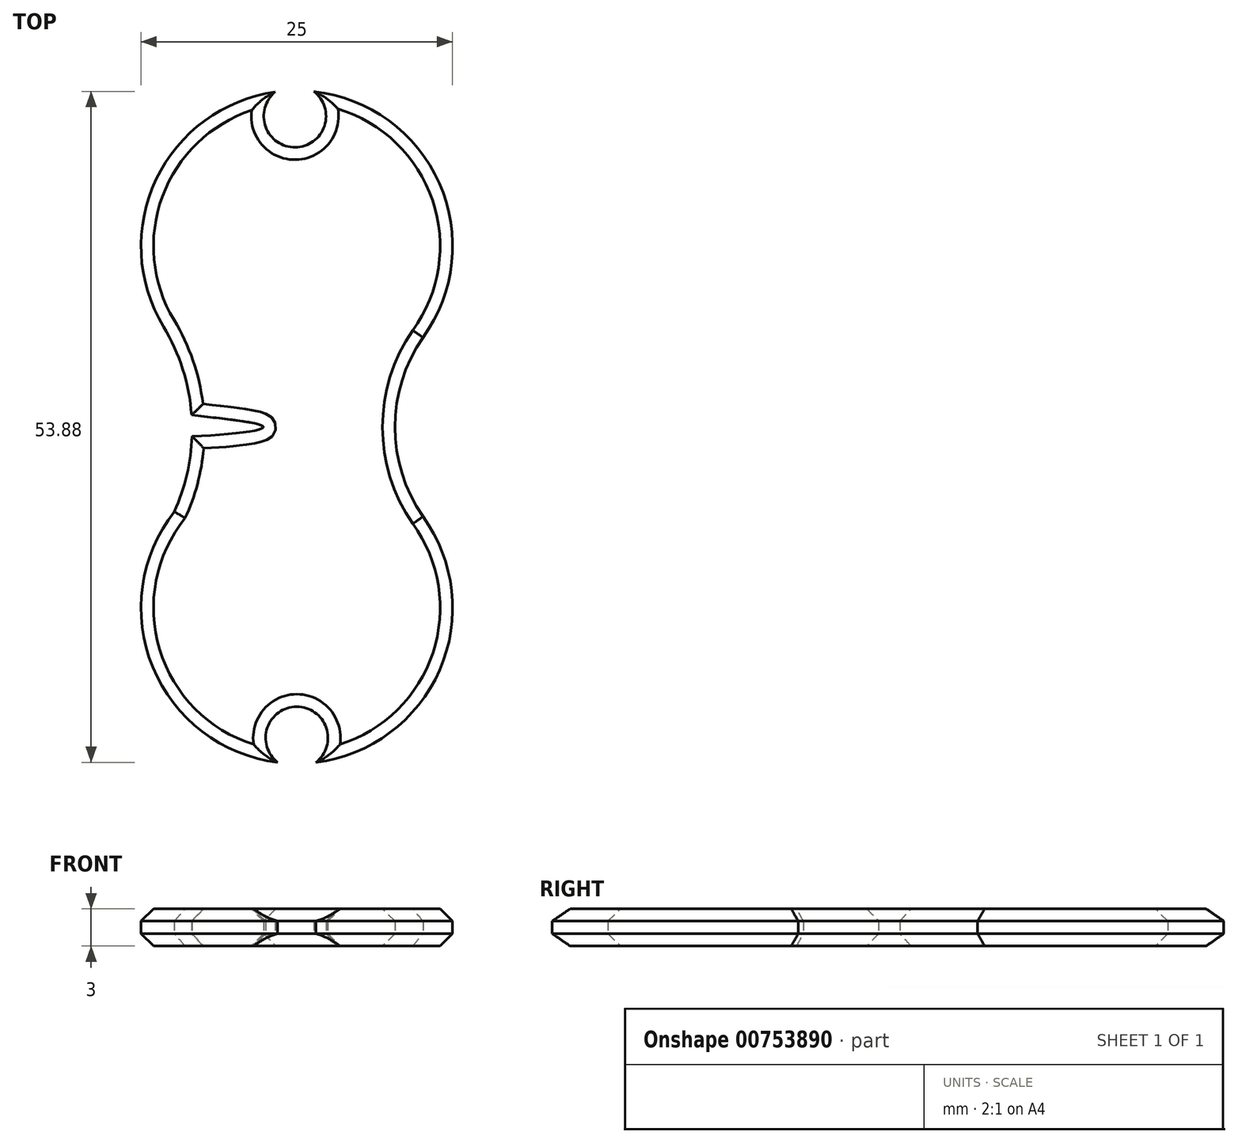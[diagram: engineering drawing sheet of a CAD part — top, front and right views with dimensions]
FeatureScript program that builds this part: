
annotation { "Feature Type Name" : "Feature", "Feature Type Description" : "" }
export const myFeature = defineFeature(function(context is Context, id is Id, definition is map)
    precondition{}
    {
        {
            var Q0;
            Q0=qCreatedBy(makeId("Top.planeOp"),FACE);
            var sketch = newSketch(context, id + "F0", { "sketchPlane" : qUnion([Q0])});
            skArc(sketch, "E0", {"start": v(10.12, 7.19) * mm, "mid": v(11.43, 19.59) * mm, "end": v(1.37, 26.95) * mm});
            skArc(sketch, "E1.MirrorC", {"start": v(10.12, -7.19) * mm, "mid": v(11.46, -19.51) * mm, "end": v(1.53, -26.93) * mm});
            skArc(sketch, "E2", {"start": v(-9.82, -6.8) * mm, "mid": v(-8.82, -3.83) * mm, "end": v(-8.41, -0.74) * mm});
            skArc(sketch, "E3.MirrorC", {"start": v(10.12, -7.19) * mm, "mid": v(8.45, -3.77) * mm, "end": v(7.88, 0) * mm});
            skPoint(sketch, "E4.start.orphan", {"position": v(0, 2.02) * mm});
            skPoint(sketch, "E5.start.orphan", {"position": v(-26.08, 0) * mm});
            skArc(sketch, "E6", {"start": v(-1.73, 26.9) * mm, "mid": v(-0.12, 22.47) * mm, "end": v(1.37, 26.95) * mm});
            skArc(sketch, "E7.trimOffspring", {"start": v(-1.73, 26.9) * mm, "mid": v(-11.29, 19.9) * mm, "end": v(-10.7, 8.07) * mm});
            skArc(sketch, "E8", {"start": v(1.53, -26.93) * mm, "mid": v(0, -22.46) * mm, "end": v(-1.53, -26.93) * mm});
            skPoint(sketch, "E8.centerSnap0", {"position": v(0, -27.02) * mm});
            skArc(sketch, "E9.trimOffspring", {"start": v(-1.53, -26.93) * mm, "mid": v(-11.56, -19.28) * mm, "end": v(-9.82, -6.8) * mm});
            skFitSpline(sketch, "E10", {"points": [v(-8.44, 0.96) * mm, v(-2.67, 0) * mm, v(-8.41, -0.74) * mm], "startDerivative": vector(17.91, -1.98) * mm, "endDerivative": vector(-17.64, -0.54) * mm});
            skArc(sketch, "E11.trimOffspring", {"start": v(-8.44, 0.96) * mm, "mid": v(-9.15, 4.65) * mm, "end": v(-10.7, 8.07) * mm});
            skArc(sketch, "E12.trimOffspring", {"start": v(7.88, 0) * mm, "mid": v(8.45, 3.77) * mm, "end": v(10.12, 7.19) * mm});
            skSolve(sketch);
        }
        {
            var Q0;
            Q0=makeQuery(id+"F0.imprint","IMPRINT",FACE,{"disambiguationData":[TD([[makeQuery(id+"F0.imprint","IMPRINT",EDGE,{"derivedFrom":sQuery(id+"F0.wireOp",EDGE,"E0")}),1.0]])]});
            extrude(context, id + "F1", {"entities" : qUnion([Q0]), "depth" : 3 * mm, "offsetDistance" : 25 * mm});
        }
        {
            var Q0;
            Q0=makeQuery(id+"F1.opExtrude","CAP_EDGE",EDGE,{"disambiguationData":[OSD([sQuery(id+"F0.wireOp",EDGE,"E7.trimOffspring")])],"isStart":false});
            var Q1;
            Q1=makeQuery(id+"F1.opExtrude","CAP_EDGE",EDGE,{"disambiguationData":[OSD([sQuery(id+"F0.wireOp",EDGE,"E6")])],"isStart":false});
            var Q2;
            Q2=makeQuery(id+"F1.opExtrude","CAP_EDGE",EDGE,{"disambiguationData":[OSD([sQuery(id+"F0.wireOp",EDGE,"E0")])],"isStart":false});
            var Q3;
            Q3=makeQuery(id+"F1.opExtrude","CAP_EDGE",EDGE,{"disambiguationData":[OSD([sQuery(id+"F0.wireOp",EDGE,"E12.trimOffspring")])],"isStart":false});
            var Q4;
            Q4=makeQuery(id+"F1.opExtrude","CAP_EDGE",EDGE,{"disambiguationData":[OSD([sQuery(id+"F0.wireOp",EDGE,"E11.trimOffspring")])],"isStart":false});
            var Q5;
            Q5=makeQuery(id+"F1.opExtrude","CAP_EDGE",EDGE,{"disambiguationData":[OSD([sQuery(id+"F0.wireOp",EDGE,"E10")])],"isStart":false});
            var Q6;
            Q6=makeQuery(id+"F1.opExtrude","CAP_EDGE",EDGE,{"disambiguationData":[OSD([sQuery(id+"F0.wireOp",EDGE,"3b38a443-56be-4acf-a088-5f6cc4ab78ee0.MirrorCS")])],"isStart":false});
            var Q7;
            Q7=makeQuery(id+"F1.opExtrude","CAP_EDGE",EDGE,{"disambiguationData":[OSD([sQuery(id+"F0.wireOp",EDGE,"E3.MirrorC")])],"isStart":false});
            var Q8;
            Q8=makeQuery(id+"F1.opExtrude","CAP_EDGE",EDGE,{"disambiguationData":[OSD([sQuery(id+"F0.wireOp",EDGE,"E1.MirrorC")])],"isStart":false});
            var Q9;
            Q9=makeQuery(id+"F1.opExtrude","CAP_EDGE",EDGE,{"disambiguationData":[OSD([sQuery(id+"F0.wireOp",EDGE,"E8")])],"isStart":false});
            var Q10;
            Q10=makeQuery(id+"F1.opExtrude","CAP_EDGE",EDGE,{"disambiguationData":[OSD([sQuery(id+"F0.wireOp",EDGE,"E9.trimOffspring")])],"isStart":false});
            var Q11;
            Q11=makeQuery(id+"F1.opExtrude","CAP_EDGE",EDGE,{"disambiguationData":[OSD([sQuery(id+"F0.wireOp",EDGE,"E2")])],"isStart":false});
            chamfer(context, id + "F2", {"entities" : qUnion([Q0, Q1, Q2, Q3, Q4, Q5, Q6, Q7, Q8, Q9, Q10, Q11]), "width" : 1 * mm, "tangentPropagation" : true});
        }
        {
            var Q0;
            Q0=makeQuery(id+"F1.opExtrude","CAP_EDGE",EDGE,{"disambiguationData":[OSD([sQuery(id+"F0.wireOp",EDGE,"E9.trimOffspring")])],"isStart":true});
            var Q1;
            Q1=makeQuery(id+"F1.opExtrude","CAP_EDGE",EDGE,{"disambiguationData":[OSD([sQuery(id+"F0.wireOp",EDGE,"E8")])],"isStart":true});
            var Q2;
            Q2=makeQuery(id+"F1.opExtrude","CAP_EDGE",EDGE,{"disambiguationData":[OSD([sQuery(id+"F0.wireOp",EDGE,"E1.MirrorC")])],"isStart":true});
            var Q3;
            Q3=makeQuery(id+"F1.opExtrude","CAP_EDGE",EDGE,{"disambiguationData":[OSD([sQuery(id+"F0.wireOp",EDGE,"E3.MirrorC")])],"isStart":true});
            var Q4;
            Q4=makeQuery(id+"F1.opExtrude","CAP_EDGE",EDGE,{"disambiguationData":[OSD([sQuery(id+"F0.wireOp",EDGE,"E2")])],"isStart":true});
            var Q5;
            Q5=makeQuery(id+"F1.opExtrude","CAP_EDGE",EDGE,{"disambiguationData":[OSD([sQuery(id+"F0.wireOp",EDGE,"E10")])],"isStart":true});
            var Q6;
            Q6=makeQuery(id+"F1.opExtrude","CAP_EDGE",EDGE,{"disambiguationData":[OSD([sQuery(id+"F0.wireOp",EDGE,"3b38a443-56be-4acf-a088-5f6cc4ab78ee0.MirrorCS")])],"isStart":true});
            var Q7;
            Q7=makeQuery(id+"F1.opExtrude","CAP_EDGE",EDGE,{"disambiguationData":[OSD([sQuery(id+"F0.wireOp",EDGE,"E12.trimOffspring")])],"isStart":true});
            var Q8;
            Q8=makeQuery(id+"F1.opExtrude","CAP_EDGE",EDGE,{"disambiguationData":[OSD([sQuery(id+"F0.wireOp",EDGE,"E11.trimOffspring")])],"isStart":true});
            var Q9;
            Q9=makeQuery(id+"F1.opExtrude","CAP_EDGE",EDGE,{"disambiguationData":[OSD([sQuery(id+"F0.wireOp",EDGE,"E7.trimOffspring")])],"isStart":true});
            var Q10;
            Q10=makeQuery(id+"F1.opExtrude","CAP_EDGE",EDGE,{"disambiguationData":[OSD([sQuery(id+"F0.wireOp",EDGE,"E6")])],"isStart":true});
            var Q11;
            Q11=makeQuery(id+"F1.opExtrude","CAP_EDGE",EDGE,{"disambiguationData":[OSD([sQuery(id+"F0.wireOp",EDGE,"E0")])],"isStart":true});
            chamfer(context, id + "F3", {"entities" : qUnion([Q0, Q1, Q2, Q3, Q4, Q5, Q6, Q7, Q8, Q9, Q10, Q11]), "width" : 1 * mm, "tangentPropagation" : true});
        }
    });
